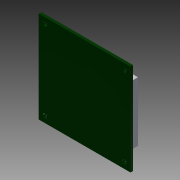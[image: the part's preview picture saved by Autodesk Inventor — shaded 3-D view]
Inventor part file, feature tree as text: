
AUTODESK INVENTOR PART (.ipt)
format: ipt  version: 2015 (Build 190159000, 159)  size: 124,416 bytes
history: native  units: in
note: dims shown in document units (in); Inventor stores cm internally (conversion verified against a paired STEP export)
features: extrude x2, sketch x2
ambient origin geometry x8: Origin, YZ Plane, XZ Plane, XY Plane, X Axis, Y Axis, Z Axis, Center Point
bodies: Solid1 (feature_tree)
feature tree (4):
  extrude  "Extrusion1"  Depth=2.25in
  extrude  "Extrusion4"  Depth=1.4567in
  sketch  "Sketch1"  dims[d0=0.0646in d1=0.0in d2=2.25in]
  sketch  "Sketch4"  dims[d4=2.25in d21=1.4567in d22=0.248in d23=0.0787in d24=0.1969in d25=0.0in d26=0.1024in d27=0.15in]
